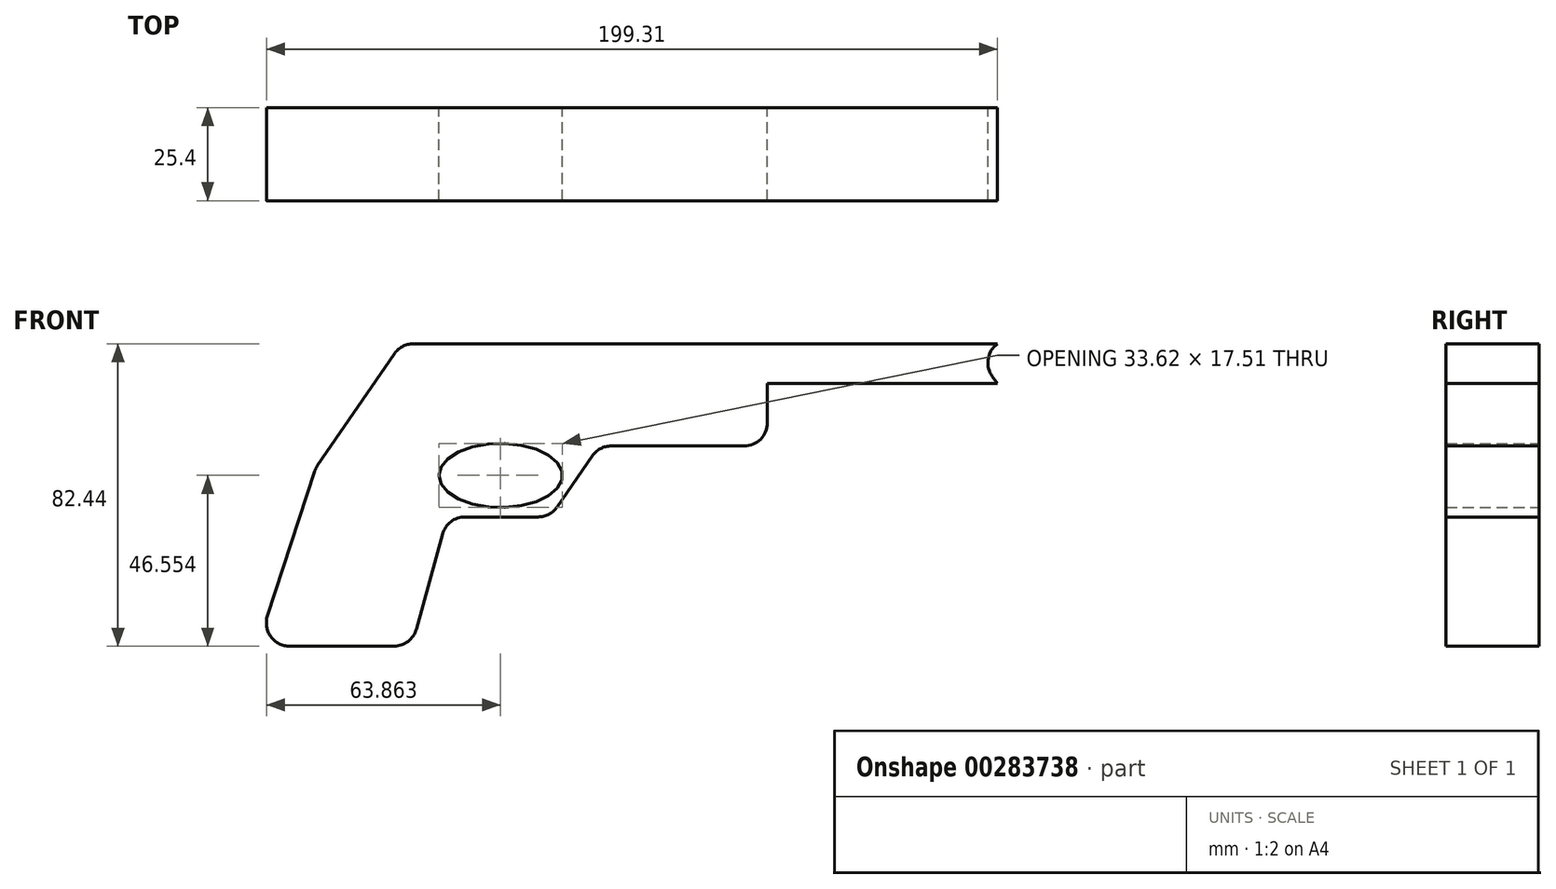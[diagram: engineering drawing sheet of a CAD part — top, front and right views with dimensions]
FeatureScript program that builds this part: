
annotation { "Feature Type Name" : "Feature", "Feature Type Description" : "" }
export const myFeature = defineFeature(function(context is Context, id is Id, definition is map)
    precondition{}
    {
        {
            var Q0;
            Q0=qCreatedBy(makeId("Front.planeOp"),FACE);
            var sketch = newSketch(context, id + "F0", { "sketchPlane" : qUnion([Q0])});
            skLineSegment(sketch, "E0", {"start": v(21.66, 30.55) * mm, "end": v(-74.89, 30.55) * mm});
            skLineSegment(sketch, "E1", {"start": v(-80.12, 27.79) * mm, "end": v(-101, -2.64) * mm});
            skLineSegment(sketch, "E2", {"start": v(-101.8, -4.26) * mm, "end": v(-114.63, -43.57) * mm});
            skLineSegment(sketch, "E3", {"start": v(-108.6, -51.89) * mm, "end": v(-80.16, -51.89) * mm});
            skLineSegment(sketch, "E4", {"start": v(-74.04, -47.22) * mm, "end": v(-66.9, -21.32) * mm});
            skLineSegment(sketch, "E5", {"start": v(-60.79, -16.65) * mm, "end": v(-40.84, -16.65) * mm});
            skLineSegment(sketch, "E6", {"start": v(-35.6, -13.9) * mm, "end": v(-26.12, -0.06) * mm});
            skLineSegment(sketch, "E7", {"start": v(-20.89, 2.7) * mm, "end": v(15.3, 2.7) * mm});
            skLineSegment(sketch, "E8", {"start": v(21.66, 9.05) * mm, "end": v(21.66, 30.55) * mm});
            skPoint(sketch, "E9.visualSharp", {"position": v(-37.5, -16.65) * mm});
            skArc(sketch, "E9.filletArc", {"start": v(-40.84, -16.65) * mm, "mid": v(-37.89, -15.92) * mm, "end": v(-35.6, -13.9) * mm});
            skPoint(sketch, "E10.visualSharp", {"position": v(-24.23, 2.7) * mm});
            skArc(sketch, "E10.filletArc", {"start": v(-20.89, 2.7) * mm, "mid": v(-23.85, 1.97) * mm, "end": v(-26.12, -0.06) * mm});
            skPoint(sketch, "E11.visualSharp", {"position": v(-65.62, -16.65) * mm});
            skArc(sketch, "E11.filletArc", {"start": v(-60.79, -16.65) * mm, "mid": v(-64.63, -17.95) * mm, "end": v(-66.9, -21.32) * mm});
            skPoint(sketch, "E12.visualSharp", {"position": v(-117.35, -51.89) * mm});
            skArc(sketch, "E12.filletArc", {"start": v(-114.63, -43.57) * mm, "mid": v(-113.73, -49.27) * mm, "end": v(-108.6, -51.89) * mm});
            skPoint(sketch, "E13.visualSharp", {"position": v(-101.5, -3.4) * mm});
            skArc(sketch, "E13.filletArc", {"start": v(-101, -2.64) * mm, "mid": v(-101.45, -3.43) * mm, "end": v(-101.8, -4.26) * mm});
            skPoint(sketch, "E14.visualSharp", {"position": v(-78.23, 30.55) * mm});
            skArc(sketch, "E14.filletArc", {"start": v(-74.89, 30.55) * mm, "mid": v(-77.85, 29.82) * mm, "end": v(-80.12, 27.79) * mm});
            skPoint(sketch, "E15.visualSharp", {"position": v(21.66, 2.7) * mm});
            skArc(sketch, "E15.filletArc", {"start": v(15.3, 2.7) * mm, "mid": v(19.8, 4.56) * mm, "end": v(21.66, 9.05) * mm});
            skLineSegment(sketch, "E16", {"start": v(21.66, 19.8) * mm, "end": v(84.37, 19.8) * mm});
            skPoint(sketch, "E16.endSnap0", {"position": v(21.66, 19.8) * mm});
            skLineSegment(sketch, "E17", {"start": v(84.37, 19.8) * mm, "end": v(83.03, 21.62) * mm});
            skLineSegment(sketch, "E18", {"start": v(83.97, 30.2) * mm, "end": v(84.37, 30.55) * mm});
            skLineSegment(sketch, "E19", {"start": v(84.37, 30.55) * mm, "end": v(21.66, 30.55) * mm});
            skPoint(sketch, "E20.visualSharp", {"position": v(79.53, 26.34) * mm});
            skArc(sketch, "E20.filletArc", {"start": v(83.97, 30.2) * mm, "mid": v(81.82, 26.1) * mm, "end": v(83.03, 21.62) * mm});
            skPoint(sketch, "E21.visualSharp", {"position": v(-75.32, -51.89) * mm});
            skArc(sketch, "E21.filletArc", {"start": v(-80.16, -51.89) * mm, "mid": v(-76.31, -50.59) * mm, "end": v(-74.04, -47.22) * mm});
            skSolve(sketch);
        }
        {
            var Q0;
            Q0=makeQuery(id+"F0.imprint","IMPRINT",FACE,{"disambiguationData":[TD([[makeQuery(id+"F0.imprint","IMPRINT",EDGE,{"derivedFrom":sQuery(id+"F0.wireOp",EDGE,"qJ8aBnEW-Kbl6-XeWB-l66D-5tdVgD6Qwl4y")}),1.0]])]});
            var Q1;
            {var subQ0=sQuery(id+"F0.wireOp",EDGE,"E16");Q1=makeQuery(id+"F0.imprint","IMPRINT",FACE,{"disambiguationData":[TD([[makeQuery(id+"F0.imprint","IMPRINT",EDGE,{"derivedFrom":subQ0}),1.0]])]});}
            var Q2;
            {var subQ1=sQuery(id+"F0.wireOp",EDGE,"E0");Q2=makeQuery(id+"F0.imprint","IMPRINT",FACE,{"disambiguationData":[TD([[makeQuery(id+"F0.imprint","IMPRINT",EDGE,{"derivedFrom":subQ1}),1.0]])]});}
            extrude(context, id + "F1", {"entities" : qUnion([Q0, Q1, Q2]), "depth" : 25.4 * mm});
        }
        {
            var Q0;
            Q0=qCreatedBy(makeId("Front.planeOp"),FACE);
            var sketch = newSketch(context, id + "F2", { "sketchPlane" : qUnion([Q0])});
            skEllipse(sketch, "E22", {"center": v(-51.08, -5.34) * mm, "majorRadius": 16.81 * mm, "minorRadius": 8.75 * mm, "majorAxis": v(-1, 0)});
            skLineSegment(sketch, "E23", {"start": v(-61.1, 1.7) * mm, "end": v(-51.5, -11.14) * mm});
            skLineSegment(sketch, "E24", {"start": v(-51.5, -11.14) * mm, "end": v(-56.3, 2.99) * mm});
            skPoint(sketch, "E24.endSnap0", {"position": v(-56.3, -4.72) * mm});
            skSolve(sketch);
        }
        {
            var Q0;
            Q0 = qSketchRegion(id + "F2", true);
            extrude(context, id + "F3", {"entities" : qUnion([Q0]), "operationType" : NewBodyOperationType.ADD, "depth" : 25.4 * mm});
        }
        {
            var Q0;
            Q0 = qSketchRegion(id + "F2", true);
            extrude(context, id + "F4", {"entities" : qUnion([Q0]), "operationType" : NewBodyOperationType.REMOVE, "depth" : 25.4 * mm});
        }
    });
